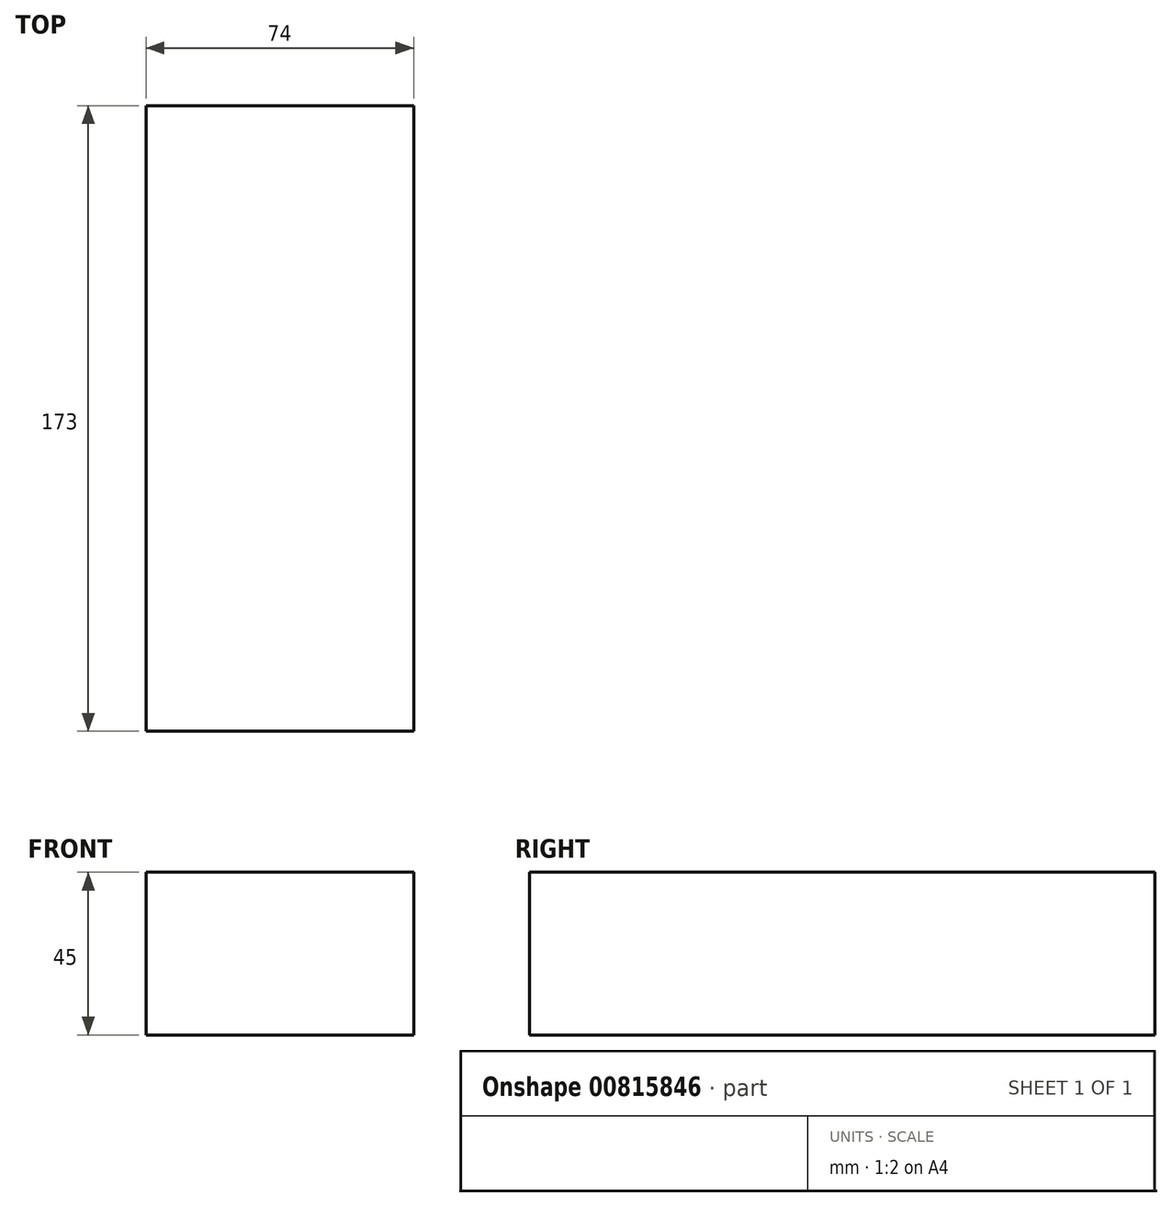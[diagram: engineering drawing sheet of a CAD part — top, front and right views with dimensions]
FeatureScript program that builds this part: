
annotation { "Feature Type Name" : "Feature", "Feature Type Description" : "" }
export const myFeature = defineFeature(function(context is Context, id is Id, definition is map)
    precondition{}
    {
        {
            var Q0;
            Q0=qCreatedBy(makeId("Front.planeOp"),FACE);
            var sketch = newSketch(context, id + "F0", { "sketchPlane" : qUnion([Q0])});
            skLineSegment(sketch, "E0.bottom", {"start": v(0, 0) * mm, "end": v(74, 0) * mm});
            skLineSegment(sketch, "E0.top", {"start": v(0, 45) * mm, "end": v(74, 45) * mm});
            skLineSegment(sketch, "E0.left", {"start": v(0, 0) * mm, "end": v(0, 45) * mm});
            skLineSegment(sketch, "E0.right", {"start": v(74, 0) * mm, "end": v(74, 45) * mm});
            skSolve(sketch);
        }
        {
            var Q0;
            Q0=makeQuery(id+"F0.imprint","IMPRINT",FACE,{"disambiguationData":[TD([[makeQuery(id+"F0.imprint","IMPRINT",EDGE,{"derivedFrom":sQuery(id+"F0.wireOp",EDGE,"E0.bottom")}),1.0]])]});
            extrude(context, id + "F1", {"entities" : qUnion([Q0]), "depth" : 173 * mm, "offsetDistance" : 25.4 * mm});
        }
    });
